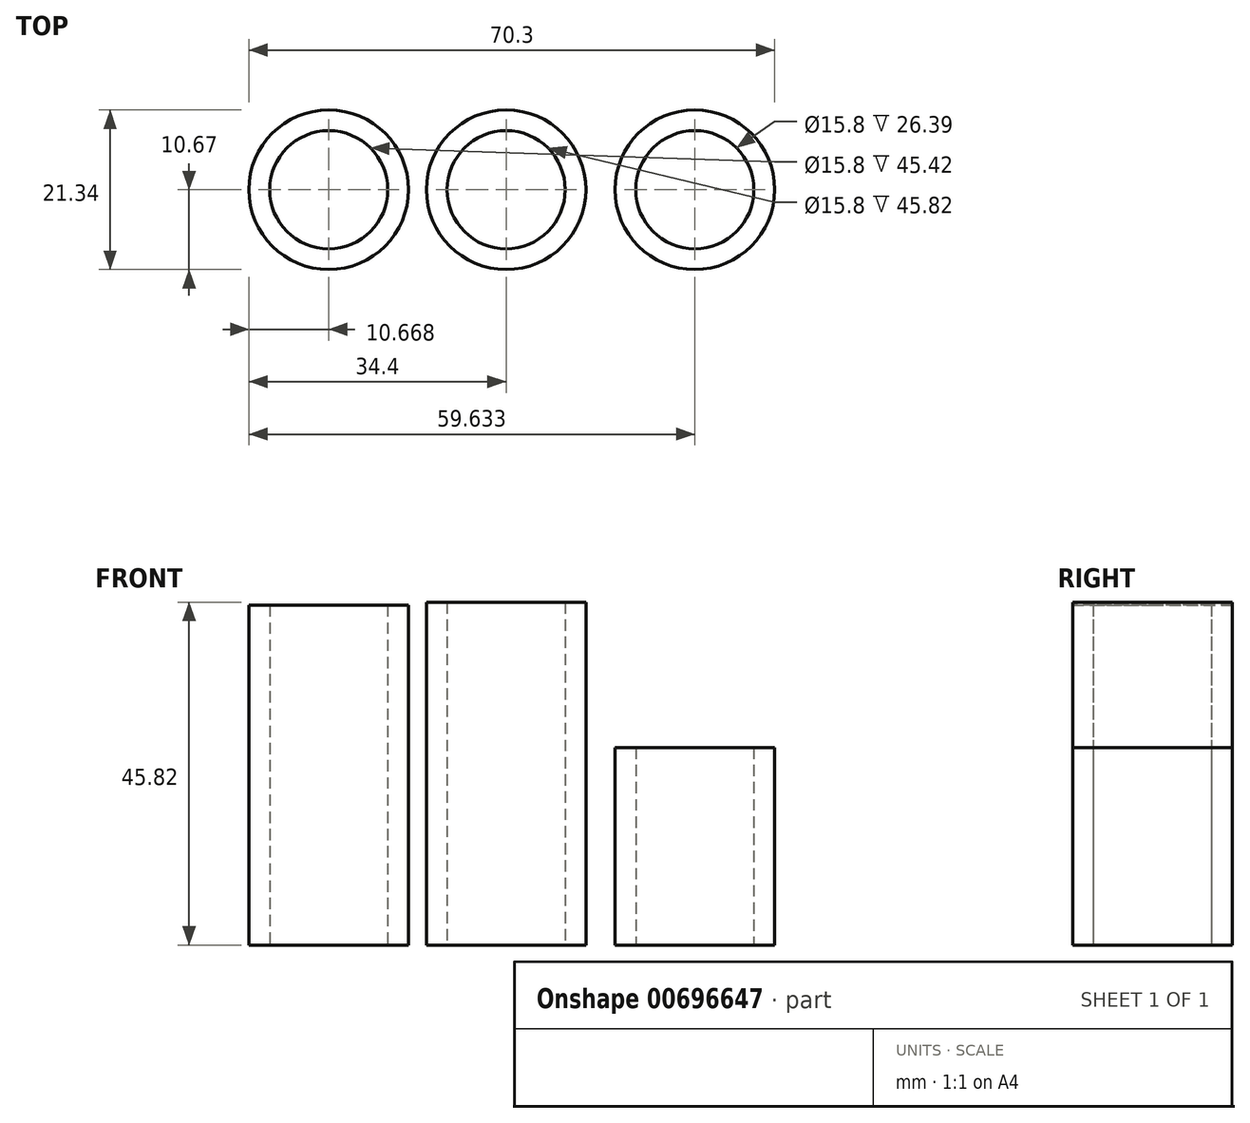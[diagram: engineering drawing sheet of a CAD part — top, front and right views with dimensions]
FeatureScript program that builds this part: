
annotation { "Feature Type Name" : "Feature", "Feature Type Description" : "" }
export const myFeature = defineFeature(function(context is Context, id is Id, definition is map)
    precondition{}
    {
        {
            var Q0;
            Q0=qCreatedBy(makeId("Top.planeOp"),FACE);
            var sketch = newSketch(context, id + "F0", { "sketchPlane" : qUnion([Q0])});
            skCircle(sketch, "E0", {"center": v(0, 0) * mm, "radius": 10.67 * mm});
            skCircle(sketch, "E1", {"center": v(0, 0) * mm, "radius": 7.9 * mm});
            skSolve(sketch);
        }
        {
            var Q0;
            Q0 = qSketchRegion(id + "F0", true);
            extrude(context, id + "F1", {"entities" : qUnion([Q0]), "depth" : 45.82 * mm, "offsetDistance" : 25 * mm});
        }
        {
            var Q0;
            Q0=qCreatedBy(makeId("Top.planeOp"),FACE);
            var sketch = newSketch(context, id + "F2", { "sketchPlane" : qUnion([Q0])});
            skCircle(sketch, "E2", {"center": v(-23.73, 0) * mm, "radius": 10.67 * mm});
            skCircle(sketch, "E3", {"center": v(-23.73, 0) * mm, "radius": 7.9 * mm});
            skSolve(sketch);
        }
        {
            var Q0;
            Q0 = qSketchRegion(id + "F2", true);
            extrude(context, id + "F3", {"entities" : qUnion([Q0]), "depth" : 45.42 * mm, "offsetDistance" : 25 * mm});
        }
        {
            var Q0;
            Q0=qCreatedBy(makeId("Top.planeOp"),FACE);
            var sketch = newSketch(context, id + "F4", { "sketchPlane" : qUnion([Q0])});
            skCircle(sketch, "E4", {"center": v(25.23, 0) * mm, "radius": 10.67 * mm});
            skCircle(sketch, "E5", {"center": v(25.23, 0) * mm, "radius": 7.9 * mm});
            skSolve(sketch);
        }
        {
            var Q0;
            Q0 = qSketchRegion(id + "F4", true);
            extrude(context, id + "F5", {"entities" : qUnion([Q0]), "depth" : 26.4 * mm, "offsetDistance" : 25 * mm});
        }
    });
